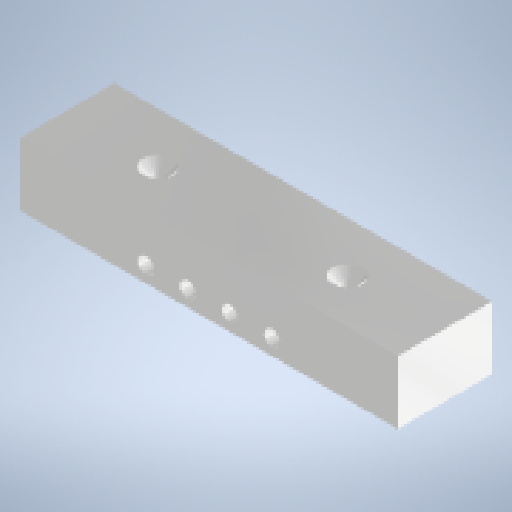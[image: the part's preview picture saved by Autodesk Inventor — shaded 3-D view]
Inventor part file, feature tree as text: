
AUTODESK INVENTOR PART (.ipt)
format: ipt  version: 2025 (Build 290162010, 162A)  size: 283,136 bytes
history: native  units: mm
features: sketch x4, hole x3, extrude x1
ambient origin geometry x8: Origin, YZ Plane, XZ Plane, XY Plane, X Axis, Y Axis, Z Axis, Center Point
bodies: Volumenkörper1 (feature_tree)
feature tree (8):
  extrude  "Extrusion1"  Depth=13.333333mm
  hole  "Bohrung1"  [1 undecoded]
  hole  "Bohrung2"  [1 undecoded]
  hole  "Bohrung3"  [1 undecoded]
  sketch  "Skizze1"  dims[d1=0.0mm d2=13.333333mm]
  sketch  "Skizze2"  dims[d3=5.0mm d5=40.0mm]
  sketch  "Skizze3"  dims[d6=1.567mm d7=8.0mm d8=4.0mm d9=2.0mm d10=90.0deg d11=10.0mm d12=20.594885mm d14=30.0mm]
  sketch  "Skizze4"  dims[d15=120.0mm d16=5.0mm d17=6.0mm d18=4.0mm d19=2.0mm d20=90.0deg d21=8.0mm d22=20.594885mm d23=60.0mm d24=5.0mm d25=60.0mm d26=14.0mm d27=4.3mm d28=12.7mm d29=9.4mm d30=2.0mm d31=90.0deg d32=8.0mm d33=20.594885mm]
note: 3 required parameter values undecoded (feature->parameter linkage not recoverable at this tier; creation-order binding heuristic only, values carry confidence <= 0.55)
